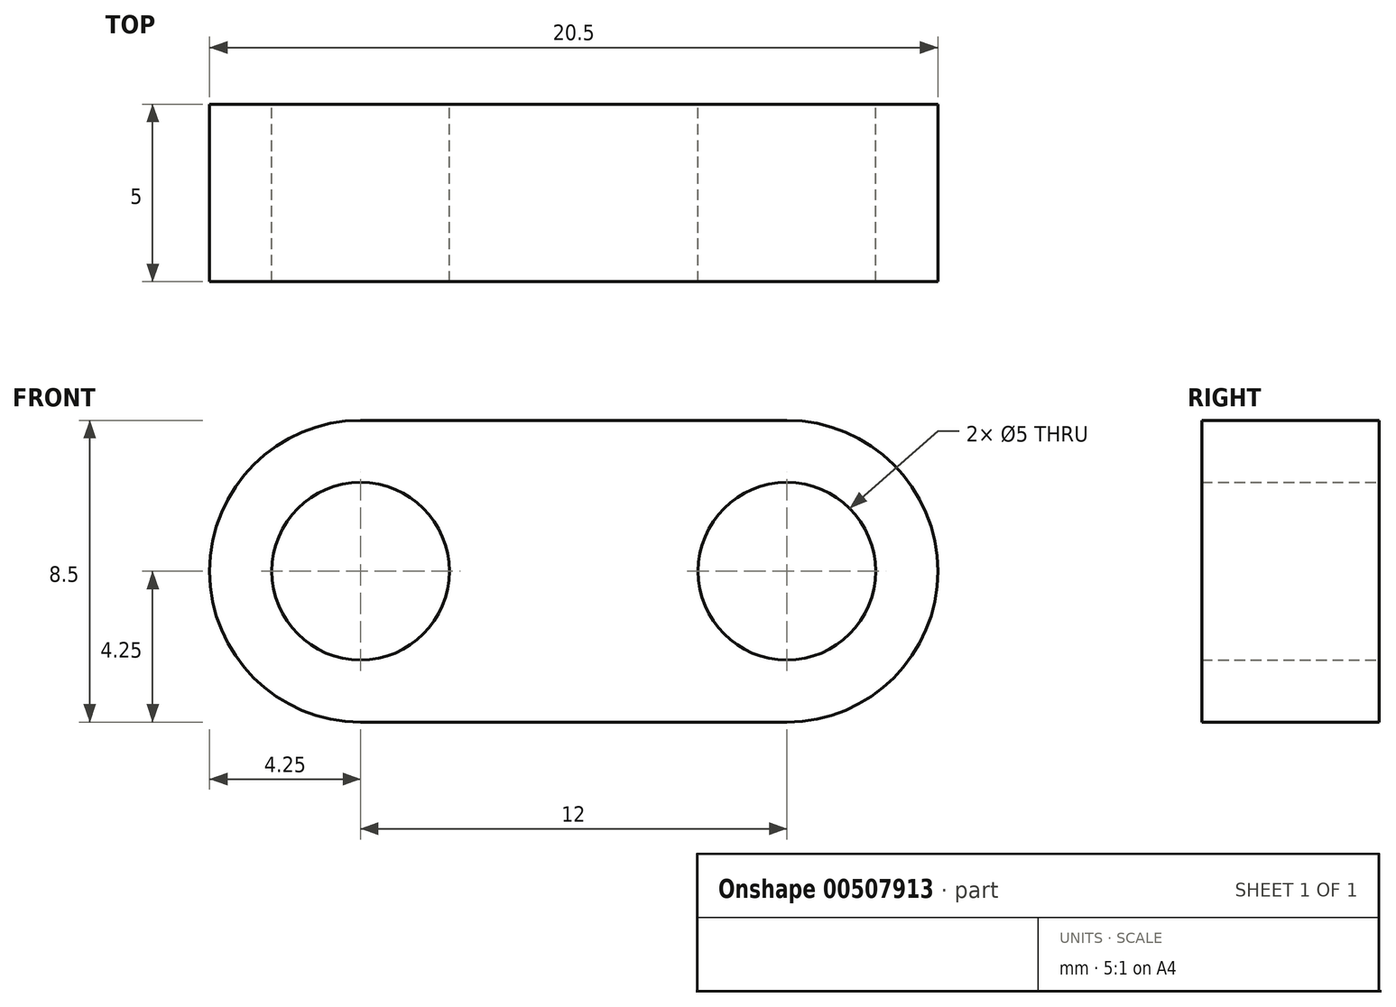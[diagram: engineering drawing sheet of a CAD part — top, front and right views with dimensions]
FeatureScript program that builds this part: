
annotation { "Feature Type Name" : "Feature", "Feature Type Description" : "" }
export const myFeature = defineFeature(function(context is Context, id is Id, definition is map)
    precondition{}
    {
        {
            var Q0;
            Q0=qCreatedBy(makeId("Front.planeOp"),FACE);
            var sketch = newSketch(context, id + "F0", { "sketchPlane" : qUnion([Q0])});
            skCircle(sketch, "E0", {"center": v(0, 0) * mm, "radius": 2.5 * mm});
            skCircle(sketch, "E1", {"center": v(0, 0) * mm, "radius": 4.25 * mm});
            skLineSegment(sketch, "E2", {"start": v(0, 0) * mm, "end": v(12, 0) * mm, "construction": true});
            skCircle(sketch, "E3", {"center": v(12, 0) * mm, "radius": 2.5 * mm});
            skCircle(sketch, "E4", {"center": v(12, 0) * mm, "radius": 4.25 * mm});
            skLineSegment(sketch, "E5", {"start": v(0, -4.25) * mm, "end": v(12, -4.25) * mm});
            skLineSegment(sketch, "E6", {"start": v(0, 4.25) * mm, "end": v(12, 4.25) * mm});
            skSolve(sketch);
        }
        {
            var Q0;
            Q0=makeQuery(id+"F0.imprint","IMPRINT",FACE,{"disambiguationData":[TD([[makeQuery(id+"F0.imprint","IMPRINT",EDGE,{"derivedFrom":sQuery(id+"F0.wireOp",EDGE,"E0")}),-1.0]])]});
            var Q1;
            Q1=makeQuery(id+"F0.imprint","IMPRINT",FACE,{"disambiguationData":[TD([[makeQuery(id+"F0.imprint","IMPRINT",EDGE,{"derivedFrom":sQuery(id+"F0.wireOp",EDGE,"E3")}),-1.0]])]});
            var Q2;
            {var subQ0=sQuery(id+"F0.wireOp",EDGE,"E5");Q2=makeQuery(id+"F0.imprint","IMPRINT",FACE,{"disambiguationData":[TD([[makeQuery(id+"F0.imprint","IMPRINT",EDGE,{"derivedFrom":subQ0}),1.0]])]});}
            extrude(context, id + "F1", {"entities" : qUnion([Q0, Q1, Q2]), "depth" : 5 * mm, "offsetDistance" : 25 * mm});
        }
    });
